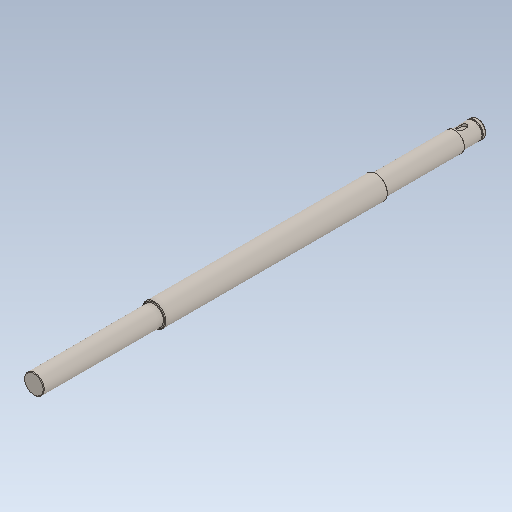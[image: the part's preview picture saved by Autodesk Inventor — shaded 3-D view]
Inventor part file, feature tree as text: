
AUTODESK INVENTOR PART (.ipt)
format: ipt  version: 2021 (Build 250183000, 183)  size: 114,176 bytes
history: mixed  units: mm
features: other x1, chamfer x1, imported_body x1
ambient origin geometry x8: Origin, YZ Plane, XZ Plane, XY Plane, X Axis, Y Axis, Z Axis, Center Point
bodies: Body1 (imported_parasolid)
feature tree (3):
  other  "Sólido1"
  chamfer  "Chamfer2"  [1 undecoded]
  imported_body  NMx_Import_Brep_tag  [imported B-rep: ~21 faces, bbox_mm=[18.5, 0.0, 381.0]]
note: 1 required parameter value undecoded (feature->parameter linkage not recoverable at this tier; creation-order binding heuristic only, values carry confidence <= 0.55)
